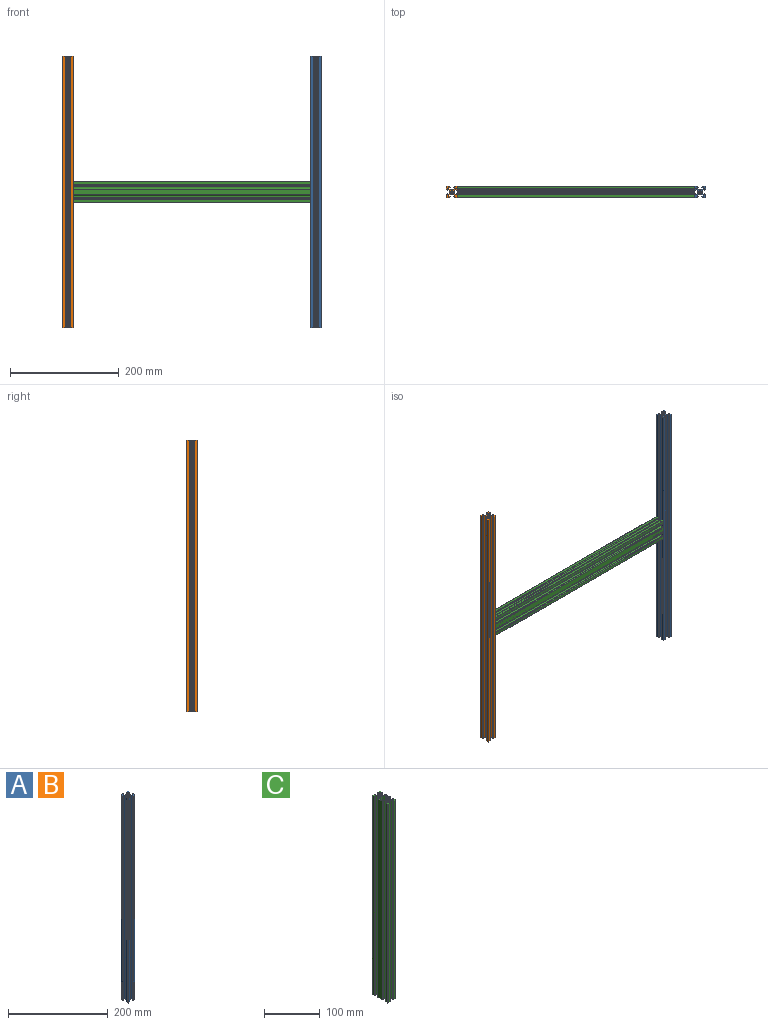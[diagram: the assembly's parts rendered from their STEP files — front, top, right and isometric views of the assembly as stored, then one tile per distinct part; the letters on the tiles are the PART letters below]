
ASSEMBLY  parts=3 mates=2
PART A: 71 faces, bbox 20x20x500 mm
  f0: plane 500x0.21mm, normal (0.71,-0.71,0), area 148.5mm2, adj f1,f67,f68,f69
  f1: plane 500x2.63mm, normal (1,0,0), area 1314.7mm2, adj f0,f2,f68,f69
  f2: plane 500x2.66mm, normal (0.71,-0.71,0), area 1881.4mm2, adj f1,f3,f68,f69
  f3: plane 500x1.64mm, normal (0,-1,0), area 819.7mm2, adj f2,f4,f68,f69
  f4: plane 500x2.38mm, normal (-1,0,0), area 1187.5mm2, adj f3,f5,f68,f69
  f5: plane 500x0.35mm, normal (0,-1,0), area 172.5mm2, adj f4,f6,f68,f69
  f6: plane 500x1.46mm, normal (0.71,-0.71,0), area 1028.8mm2, adj f5,f7,f68,f69
  f7: plane 500x4.92mm, normal (1,0,0), area 2460mm2, adj f6,f8,f68,f69
  f8: cylinder r=0.5mm len=500mm, axis (0,0,-1), area 392.7mm2, adj f7,f9,f68,f69
  f9: plane 500x4.92mm, normal (0,1,0), area 2460mm2, adj f8,f10,f68,f69
  f10: plane 500x1.46mm, normal (-0.71,0.71,0), area 1028.8mm2, adj f9,f11,f68,f69
  f11: plane 500x0.35mm, normal (-1,0,0), area 172.5mm2, adj f10,f12,f68,f69
  f12: plane 500x2.38mm, normal (0,-1,0), area 1187.5mm2, adj f11,f13,f68,f69
  f13: plane 500x1.64mm, normal (-1,0,0), area 819.7mm2, adj f12,f14,f68,f69
  f14: plane 500x2.66mm, normal (-0.71,0.71,0), area 1881.4mm2, adj f13,f15,f68,f69
  f15: plane 500x2.63mm, normal (0,1,0), area 1314.7mm2, adj f14,f16,f68,f69
  f16: plane 500x0.21mm, normal (-0.71,0.71,0), area 148.5mm2, adj f15,f17,f68,f69
  f17: plane 500x0.21mm, normal (0.71,0.71,0), area 148.5mm2, adj f16,f18,f68,f69
  f18: plane 500x2.63mm, normal (0,1,0), area 1314.7mm2, adj f17,f19,f68,f69
  f19: plane 500x2.66mm, normal (0.71,0.71,0), area 1881.4mm2, adj f18,f20,f68,f69
  f20: plane 500x1.64mm, normal (1,0,0), area 819.7mm2, adj f19,f21,f68,f69
  f21: plane 500x2.38mm, normal (0,-1,0), area 1187.5mm2, adj f20,f22,f68,f69
  f22: plane 500x0.35mm, normal (1,0,0), area 172.5mm2, adj f21,f23,f68,f69
  f23: plane 500x1.46mm, normal (0.71,0.71,0), area 1028.8mm2, adj f22,f24,f68,f69
  f24: plane 500x4.92mm, normal (0,1,0), area 2460mm2, adj f23,f25,f68,f69
  f25: cylinder r=0.5mm len=500mm, axis (0,0,-1), area 392.7mm2, adj f24,f26,f68,f69
  f26: plane 500x4.92mm, normal (-1,0,0), area 2460mm2, adj f25,f27,f68,f69
  f27: plane 500x1.46mm, normal (-0.71,-0.71,0), area 1028.8mm2, adj f26,f28,f68,f69
  f28: plane 500x0.35mm, normal (0,-1,0), area 172.5mm2, adj f27,f29,f68,f69
  f29: plane 500x2.38mm, normal (1,0,0), area 1187.5mm2, adj f28,f30,f68,f69
  f30: plane 500x1.64mm, normal (0,-1,0), area 819.7mm2, adj f29,f31,f68,f69
  f31: plane 500x2.66mm, normal (-0.71,-0.71,0), area 1881.4mm2, adj f30,f32,f68,f69
  f32: plane 500x2.63mm, normal (-1,0,0), area 1314.7mm2, adj f31,f33,f68,f69
  f33: plane 500x0.21mm, normal (-0.71,-0.71,0), area 148.5mm2, adj f32,f34,f68,f69
  f34: plane 500x0.21mm, normal (-0.71,0.71,0), area 148.5mm2, adj f33,f35,f68,f69
  f35: plane 500x2.63mm, normal (-1,0,0), area 1314.7mm2, adj f34,f36,f68,f69
  f36: plane 500x2.66mm, normal (-0.71,0.71,0), area 1881.4mm2, adj f35,f37,f68,f69
  f37: plane 500x1.64mm, normal (0,1,0), area 819.7mm2, adj f36,f38,f68,f69
  f38: plane 500x2.38mm, normal (1,0,0), area 1187.5mm2, adj f37,f39,f68,f69
  f39: plane 500x0.35mm, normal (0,1,0), area 172.5mm2, adj f38,f40,f68,f69
  f40: plane 500x1.46mm, normal (-0.71,0.71,0), area 1028.8mm2, adj f39,f41,f68,f69
  f41: plane 500x4.92mm, normal (-1,0,0), area 2460mm2, adj f40,f42,f68,f69
  f42: cylinder r=0.5mm len=500mm, axis (0,0,-1), area 392.7mm2, adj f41,f43,f68,f69
  f43: plane 500x4.92mm, normal (0,-1,0), area 2460mm2, adj f42,f44,f68,f69
  f44: plane 500x1.46mm, normal (0.71,-0.71,0), area 1028.8mm2, adj f43,f45,f68,f69
  f45: plane 500x0.35mm, normal (1,0,0), area 172.5mm2, adj f44,f46,f68,f69
  f46: plane 500x2.38mm, normal (0,1,0), area 1187.5mm2, adj f45,f47,f68,f69
  f47: plane 500x1.64mm, normal (1,0,0), area 819.7mm2, adj f46,f48,f68,f69
  f48: plane 500x2.66mm, normal (0.71,-0.71,0), area 1881.4mm2, adj f47,f49,f68,f69
  f49: plane 500x2.63mm, normal (0,-1,0), area 1314.7mm2, adj f48,f50,f68,f69
  f50: plane 500x0.21mm, normal (0.71,-0.71,0), area 148.5mm2, adj f49,f51,f68,f69
  f51: plane 500x0.21mm, normal (-0.71,-0.71,0), area 148.5mm2, adj f50,f52,f68,f69
  f52: plane 500x2.63mm, normal (0,-1,0), area 1314.7mm2, adj f51,f53,f68,f69
  f53: plane 500x2.66mm, normal (-0.71,-0.71,0), area 1881.4mm2, adj f52,f54,f68,f69
  f54: plane 500x1.64mm, normal (-1,0,0), area 819.7mm2, adj f53,f55,f68,f69
  f55: plane 500x2.38mm, normal (0,1,0), area 1187.5mm2, adj f54,f56,f68,f69
  f56: plane 500x0.35mm, normal (-1,0,0), area 172.5mm2, adj f55,f57,f68,f69
  f57: plane 500x1.46mm, normal (-0.71,-0.71,0), area 1028.8mm2, adj f56,f58,f68,f69
  f58: plane 500x4.92mm, normal (0,-1,0), area 2460mm2, adj f57,f59,f68,f69
  f59: cylinder r=0.5mm len=500mm, axis (0,0,-1), area 392.7mm2, adj f58,f60,f68,f69
  f60: plane 500x4.92mm, normal (1,0,0), area 2460mm2, adj f59,f61,f68,f69
  f61: plane 500x1.46mm, normal (0.71,0.71,0), area 1028.8mm2, adj f60,f62,f68,f69
  f62: plane 500x0.35mm, normal (0,1,0), area 172.5mm2, adj f61,f63,f68,f69
  f63: plane 500x2.38mm, normal (-1,0,0), area 1187.5mm2, adj f62,f64,f68,f69
  f64: plane 500x1.64mm, normal (0,1,0), area 819.7mm2, adj f63,f65,f68,f69
  f65: plane 500x2.66mm, normal (0.71,0.71,0), area 1881.4mm2, adj f64,f66,f68,f69
  f66: plane 500x2.63mm, normal (1,0,0), area 1314.7mm2, adj f65,f67,f68,f69
  f67: plane 500x0.21mm, normal (0.71,0.71,0), area 148.5mm2, adj f0,f66,f68,f69
  f68: plane 20x20mm, normal (0,0,1), area 171.4mm2, adj f0,f1,f2,f3,f4,f5,f6,f7
  f69: plane 20x20mm, normal (0,0,-1), area 171.4mm2, adj f0,f1,f2,f3,f4,f5,f6,f7
  f70: cylinder r=2.1mm len=500mm, axis (0,0,-1), area 6597.3mm2, adj f68,f69
PART B: same geometry as A
PART C: 114 faces, bbox 20x40x436.6 mm
  f0: plane 436.56x0.21mm, normal (0.71,-0.71,0), area 129.7mm2, adj f1,f105,f112,f113
  f1: plane 436.56x2.63mm, normal (1,0,0), area 1147.9mm2, adj f0,f2,f112,f113
  f2: plane 436.56x2.66mm, normal (0.71,-0.71,0), area 1642.7mm2, adj f1,f3,f112,f113
  f3: plane 436.56x1.64mm, normal (0,-1,0), area 715.7mm2, adj f2,f4,f112,f113
  f4: plane 436.56x2.38mm, normal (-1,0,0), area 1036.8mm2, adj f3,f5,f112,f113
  f5: plane 436.56x0.35mm, normal (0,-1,0), area 150.6mm2, adj f4,f6,f112,f113
  f6: plane 436.56x1.46mm, normal (0.71,-0.71,0), area 898.3mm2, adj f5,f7,f112,f113
  f7: plane 436.56x4.92mm, normal (1,0,0), area 2147.9mm2, adj f6,f8,f112,f113
  f8: cylinder r=0.5mm len=436.56mm, axis (0,0,-1), area 342.9mm2, adj f7,f9,f112,f113
  f9: plane 436.56x4.92mm, normal (0,1,0), area 2147.9mm2, adj f8,f59,f112,f113
  f10: plane 436.56x0.21mm, normal (0.71,0.71,0), area 129.7mm2, adj f11,f65,f112,f113
  f11: plane 436.56x2.63mm, normal (0,1,0), area 1147.9mm2, adj f10,f12,f112,f113
  f12: plane 436.56x2.66mm, normal (0.71,0.71,0), area 1642.7mm2, adj f11,f13,f112,f113
  f13: plane 436.56x1.64mm, normal (1,0,0), area 715.7mm2, adj f12,f14,f112,f113
  f14: plane 436.56x2.38mm, normal (0,-1,0), area 1036.8mm2, adj f13,f15,f112,f113
  f15: plane 436.56x0.35mm, normal (1,0,0), area 150.6mm2, adj f14,f16,f112,f113
  f16: plane 436.56x1.46mm, normal (0.71,0.71,0), area 898.3mm2, adj f15,f17,f112,f113
  f17: plane 436.56x4.92mm, normal (0,1,0), area 2147.9mm2, adj f16,f18,f112,f113
  f18: cylinder r=0.5mm len=436.56mm, axis (0,0,-1), area 342.9mm2, adj f17,f66,f112,f113
  f19: plane 436.56x0.21mm, normal (-0.71,0.71,0), area 129.7mm2, adj f20,f73,f112,f113
  f20: plane 436.56x2.63mm, normal (-1,0,0), area 1147.9mm2, adj f19,f21,f112,f113
  f21: plane 436.56x2.66mm, normal (-0.71,0.71,0), area 1642.7mm2, adj f20,f22,f112,f113
  f22: plane 436.56x1.64mm, normal (0,1,0), area 715.7mm2, adj f21,f23,f112,f113
  f23: plane 436.56x2.38mm, normal (1,0,0), area 1036.8mm2, adj f22,f24,f112,f113
  f24: plane 436.56x0.35mm, normal (0,1,0), area 150.6mm2, adj f23,f25,f112,f113
  f25: plane 436.56x1.46mm, normal (-0.71,0.71,0), area 898.3mm2, adj f24,f74,f112,f113
  f26: plane 436.56x0.21mm, normal (-0.71,0.71,0), area 129.7mm2, adj f27,f81,f112,f113
  f27: plane 436.56x2.63mm, normal (-1,0,0), area 1147.9mm2, adj f26,f28,f112,f113
  f28: plane 436.56x2.66mm, normal (-0.71,0.71,0), area 1642.7mm2, adj f27,f29,f112,f113
  f29: plane 436.56x1.64mm, normal (0,1,0), area 715.7mm2, adj f28,f30,f112,f113
  f30: plane 436.56x2.38mm, normal (1,0,0), area 1036.8mm2, adj f29,f31,f112,f113
  f31: plane 436.56x0.35mm, normal (0,1,0), area 150.6mm2, adj f30,f32,f112,f113
  f32: plane 436.56x1.46mm, normal (-0.71,0.71,0), area 898.3mm2, adj f31,f82,f112,f113
  f33: cylinder r=0.5mm len=436.56mm, axis (0,0,-1), area 342.9mm2, adj f82,f83,f112,f113
  f34: plane 436.56x0.21mm, normal (-0.71,-0.71,0), area 129.7mm2, adj f35,f90,f112,f113
  f35: plane 436.56x2.63mm, normal (0,-1,0), area 1147.9mm2, adj f34,f36,f112,f113
  f36: plane 436.56x2.66mm, normal (-0.71,-0.71,0), area 1642.7mm2, adj f35,f37,f112,f113
  f37: plane 436.56x1.64mm, normal (-1,0,0), area 715.7mm2, adj f36,f38,f112,f113
  f38: plane 436.56x2.38mm, normal (0,1,0), area 1036.8mm2, adj f37,f39,f112,f113
  f39: plane 436.56x0.35mm, normal (-1,0,0), area 150.6mm2, adj f38,f40,f112,f113
  f40: plane 436.56x1.46mm, normal (-0.71,-0.71,0), area 898.3mm2, adj f39,f91,f112,f113
  f41: cylinder r=0.5mm len=436.56mm, axis (0,0,-1), area 342.9mm2, adj f42,f91,f112,f113
  f42: plane 436.56x4.92mm, normal (1,0,0), area 2147.9mm2, adj f41,f92,f112,f113
  f43: plane 436.56x0.21mm, normal (0.71,-0.71,0), area 129.7mm2, adj f44,f98,f112,f113
  f44: plane 436.56x2.63mm, normal (1,0,0), area 1147.9mm2, adj f43,f45,f112,f113
  f45: plane 436.56x2.66mm, normal (0.71,-0.71,0), area 1642.7mm2, adj f44,f46,f112,f113
  f46: plane 436.56x1.64mm, normal (0,-1,0), area 715.7mm2, adj f45,f47,f112,f113
  f47: plane 436.56x2.38mm, normal (-1,0,0), area 1036.8mm2, adj f46,f48,f112,f113
  f48: plane 436.56x0.35mm, normal (0,-1,0), area 150.6mm2, adj f47,f49,f112,f113
  f49: plane 436.56x1.46mm, normal (0.71,-0.71,0), area 898.3mm2, adj f48,f50,f112,f113
  f50: plane 436.56x10.84mm, normal (1,0,0), area 4732.3mm2, adj f49,f99,f112,f113
  f51: plane 436.56x5.4mm, normal (1,0,0), area 2357.4mm2, adj f52,f111,f112,f113
  f52: plane 436.56x1.96mm, normal (0,-1,0), area 855.9mm2, adj f51,f53,f112,f113
  f53: plane 436.56x3.4mm, normal (0.71,-0.71,0), area 2099.1mm2, adj f52,f54,f112,f113
  f54: plane 436.56x5.68mm, normal (0,-1,0), area 2479.1mm2, adj f53,f106,f112,f113
  f55: plane 436.56x1.96mm, normal (0,1,0), area 855.9mm2, adj f56,f108,f112,f113
  f56: plane 436.56x3.4mm, normal (-0.71,0.71,0), area 2099.1mm2, adj f55,f109,f112,f113
  f57: cylinder r=2.1mm len=436.56mm, axis (0,0,-1), area 5760.3mm2, adj f112,f113
  f58: cylinder r=2.1mm len=436.56mm, axis (0,0,-1), area 5760.3mm2, adj f112,f113
  f59: plane 436.56x1.46mm, normal (-0.71,0.71,0), area 898.3mm2, adj f9,f60,f112,f113
  f60: plane 436.56x0.35mm, normal (-1,0,0), area 150.6mm2, adj f59,f61,f112,f113
  f61: plane 436.56x2.38mm, normal (0,-1,0), area 1036.8mm2, adj f60,f62,f112,f113
  f62: plane 436.56x1.64mm, normal (-1,0,0), area 715.7mm2, adj f61,f63,f112,f113
  f63: plane 436.56x2.66mm, normal (-0.71,0.71,0), area 1642.7mm2, adj f62,f64,f112,f113
  f64: plane 436.56x2.63mm, normal (0,1,0), area 1147.9mm2, adj f63,f65,f112,f113
  f65: plane 436.56x0.21mm, normal (-0.71,0.71,0), area 129.7mm2, adj f10,f64,f112,f113
  f66: plane 436.56x4.92mm, normal (-1,0,0), area 2147.9mm2, adj f18,f67,f112,f113
  f67: plane 436.56x1.46mm, normal (-0.71,-0.71,0), area 898.3mm2, adj f66,f68,f112,f113
  f68: plane 436.56x0.35mm, normal (0,-1,0), area 150.6mm2, adj f67,f69,f112,f113
  f69: plane 436.56x2.38mm, normal (1,0,0), area 1036.8mm2, adj f68,f70,f112,f113
  f70: plane 436.56x1.64mm, normal (0,-1,0), area 715.7mm2, adj f69,f71,f112,f113
  f71: plane 436.56x2.66mm, normal (-0.71,-0.71,0), area 1642.7mm2, adj f70,f72,f112,f113
  f72: plane 436.56x2.63mm, normal (-1,0,0), area 1147.9mm2, adj f71,f73,f112,f113
  f73: plane 436.56x0.21mm, normal (-0.71,-0.71,0), area 129.7mm2, adj f19,f72,f112,f113
  f74: plane 436.56x10.84mm, normal (-1,0,0), area 4732.3mm2, adj f25,f75,f112,f113
  f75: plane 436.56x1.46mm, normal (-0.71,-0.71,0), area 898.3mm2, adj f74,f76,f112,f113
  f76: plane 436.56x0.35mm, normal (0,-1,0), area 150.6mm2, adj f75,f77,f112,f113
  f77: plane 436.56x2.38mm, normal (1,0,0), area 1036.8mm2, adj f76,f78,f112,f113
  f78: plane 436.56x1.64mm, normal (0,-1,0), area 715.7mm2, adj f77,f79,f112,f113
  f79: plane 436.56x2.66mm, normal (-0.71,-0.71,0), area 1642.7mm2, adj f78,f80,f112,f113
  f80: plane 436.56x2.63mm, normal (-1,0,0), area 1147.9mm2, adj f79,f81,f112,f113
  f81: plane 436.56x0.21mm, normal (-0.71,-0.71,0), area 129.7mm2, adj f26,f80,f112,f113
  f82: plane 436.56x4.92mm, normal (-1,0,0), area 2147.9mm2, adj f32,f33,f112,f113
  f83: plane 436.56x4.92mm, normal (0,-1,0), area 2147.9mm2, adj f33,f84,f112,f113
  f84: plane 436.56x1.46mm, normal (0.71,-0.71,0), area 898.3mm2, adj f83,f85,f112,f113
  f85: plane 436.56x0.35mm, normal (1,0,0), area 150.6mm2, adj f84,f86,f112,f113
  f86: plane 436.56x2.38mm, normal (0,1,0), area 1036.8mm2, adj f85,f87,f112,f113
  f87: plane 436.56x1.64mm, normal (1,0,0), area 715.7mm2, adj f86,f88,f112,f113
  f88: plane 436.56x2.66mm, normal (0.71,-0.71,0), area 1642.7mm2, adj f87,f89,f112,f113
  f89: plane 436.56x2.63mm, normal (0,-1,0), area 1147.9mm2, adj f88,f90,f112,f113
  f90: plane 436.56x0.21mm, normal (0.71,-0.71,0), area 129.7mm2, adj f34,f89,f112,f113
  f91: plane 436.56x4.92mm, normal (0,-1,0), area 2147.9mm2, adj f40,f41,f112,f113
  f92: plane 436.56x1.46mm, normal (0.71,0.71,0), area 898.3mm2, adj f42,f93,f112,f113
  f93: plane 436.56x0.35mm, normal (0,1,0), area 150.6mm2, adj f92,f94,f112,f113
  f94: plane 436.56x2.38mm, normal (-1,0,0), area 1036.8mm2, adj f93,f95,f112,f113
  f95: plane 436.56x1.64mm, normal (0,1,0), area 715.7mm2, adj f94,f96,f112,f113
  f96: plane 436.56x2.66mm, normal (0.71,0.71,0), area 1642.7mm2, adj f95,f97,f112,f113
  f97: plane 436.56x2.63mm, normal (1,0,0), area 1147.9mm2, adj f96,f98,f112,f113
  f98: plane 436.56x0.21mm, normal (0.71,0.71,0), area 129.7mm2, adj f43,f97,f112,f113
  f99: plane 436.56x1.46mm, normal (0.71,0.71,0), area 898.3mm2, adj f50,f100,f112,f113
  f100: plane 436.56x0.35mm, normal (0,1,0), area 150.6mm2, adj f99,f101,f112,f113
  f101: plane 436.56x2.38mm, normal (-1,0,0), area 1036.8mm2, adj f100,f102,f112,f113
  f102: plane 436.56x1.64mm, normal (0,1,0), area 715.7mm2, adj f101,f103,f112,f113
  f103: plane 436.56x2.66mm, normal (0.71,0.71,0), area 1642.7mm2, adj f102,f104,f112,f113
  f104: plane 436.56x2.63mm, normal (1,0,0), area 1147.9mm2, adj f103,f105,f112,f113
  f105: plane 436.56x0.21mm, normal (0.71,0.71,0), area 129.7mm2, adj f0,f104,f112,f113
  f106: plane 436.56x3.4mm, normal (-0.71,-0.71,0), area 2099.1mm2, adj f54,f107,f112,f113
  f107: plane 436.56x1.96mm, normal (0,-1,0), area 855.9mm2, adj f106,f108,f112,f113
  f108: plane 436.56x5.4mm, normal (-1,0,0), area 2357.4mm2, adj f55,f107,f112,f113
  f109: plane 436.56x5.68mm, normal (0,1,0), area 2479.1mm2, adj f56,f110,f112,f113
  f110: plane 436.56x3.4mm, normal (0.71,0.71,0), area 2099.1mm2, adj f109,f111,f112,f113
  f111: plane 436.56x1.96mm, normal (0,1,0), area 855.9mm2, adj f51,f110,f112,f113
  f112: plane 40x20mm, normal (0,0,-1), area 300mm2, adj f0,f1,f2,f3,f4,f5,f6,f7
  f113: plane 40x20mm, normal (0,0,1), area 300mm2, adj f0,f1,f2,f3,f4,f5,f6,f7
PLACE A t=(267.65,35.73,-32.8)mm
PLACE B t=(-188.91,35.73,-32.8)mm
PLACE C rot(axis=(0.58,-0.58,-0.58),120deg) t=(257.65,35.73,217.2)mm
MATE fastened C.f113 <-> B.f60  axis (-1,0,0) through (-178.91,25.73,217.2)mm
MATE fastened A.f26 <-> C.f112  axis (-1,0,0) through (257.65,45.23,217.2)mm
